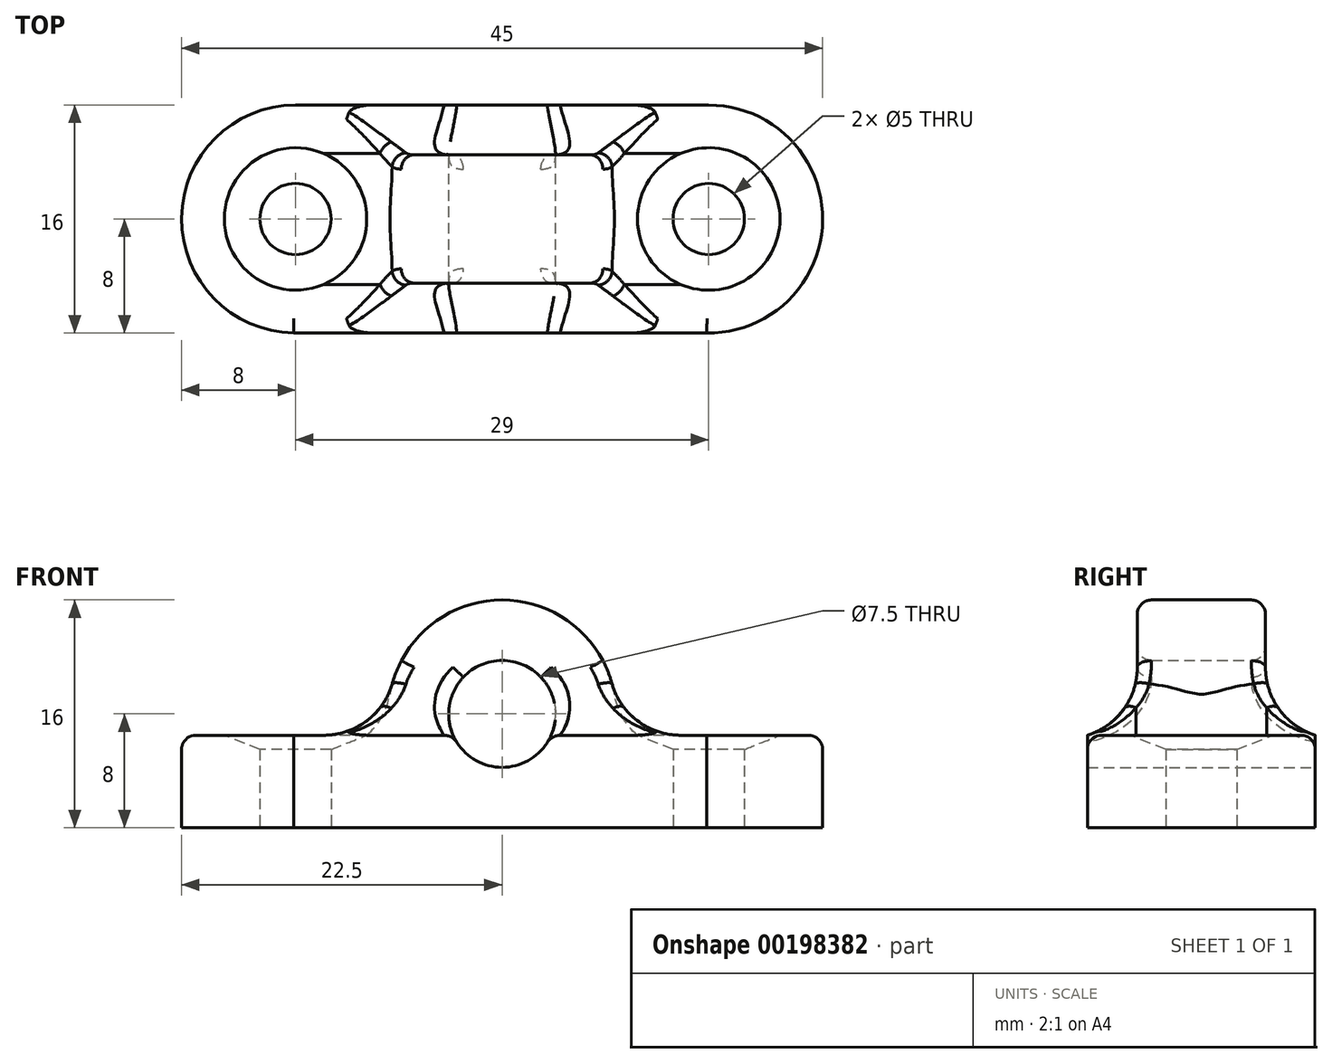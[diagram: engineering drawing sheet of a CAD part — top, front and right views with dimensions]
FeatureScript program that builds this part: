
annotation { "Feature Type Name" : "Feature", "Feature Type Description" : "" }
export const myFeature = defineFeature(function(context is Context, id is Id, definition is map)
    precondition{}
    {
        {
            var Q0;
            Q0=qCreatedBy(makeId("Top.planeOp"),FACE);
            var sketch = newSketch(context, id + "F0", { "sketchPlane" : qUnion([Q0])});
            skCircle(sketch, "E0", {"center": v(-14.5, 0) * mm, "radius": 2.5 * mm});
            skCircle(sketch, "E1", {"center": v(14.5, 0) * mm, "radius": 2.5 * mm});
            skCircle(sketch, "E2", {"center": v(-14.5, 0) * mm, "radius": 8 * mm});
            skCircle(sketch, "E3", {"center": v(14.5, 0) * mm, "radius": 8 * mm});
            skLineSegment(sketch, "E4", {"start": v(-14.63, -8) * mm, "end": v(14.37, -8) * mm});
            skLineSegment(sketch, "E5", {"start": v(-14.5, 8) * mm, "end": v(14.5, 8) * mm});
            skSolve(sketch);
        }
        {
            var Q0;
            Q0=makeQuery(id+"F0.imprint","IMPRINT",FACE,{"disambiguationData":[TD([[makeQuery(id+"F0.imprint","IMPRINT",EDGE,{"derivedFrom":sQuery(id+"F0.wireOp",EDGE,"E0")}),-1.0]])]});
            var Q1;
            {var subQ0=sQuery(id+"F0.wireOp",EDGE,"E5");Q1=makeQuery(id+"F0.imprint","IMPRINT",FACE,{"disambiguationData":[TD([[makeQuery(id+"F0.imprint","IMPRINT",EDGE,{"derivedFrom":subQ0}),-1.0]])]});}
            var Q2;
            Q2=makeQuery(id+"F0.imprint","IMPRINT",FACE,{"disambiguationData":[TD([[makeQuery(id+"F0.imprint","IMPRINT",EDGE,{"derivedFrom":sQuery(id+"F0.wireOp",EDGE,"E1")}),-1.0]])]});
            extrude(context, id + "F1", {"entities" : qUnion([Q0, Q1, Q2]), "depth" : 6.5 * mm});
        }
        {
            var Q0;
            Q0=qCreatedBy(makeId("Front.planeOp"),FACE);
            var sketch = newSketch(context, id + "F2", { "sketchPlane" : qUnion([Q0])});
            skPoint(sketch, "E6", {"position": v(0, 8) * mm});
            skCircle(sketch, "E7", {"center": v(0, 8) * mm, "radius": 8 * mm});
            skCircle(sketch, "E8", {"center": v(0, 8) * mm, "radius": 3.75 * mm});
            skSolve(sketch);
        }
        {
            var Q0;
            Q0=makeQuery(id+"F2.imprint","IMPRINT",FACE,{"disambiguationData":[TD([[makeQuery(id+"F2.imprint","IMPRINT",EDGE,{"derivedFrom":sQuery(id+"F2.wireOp",EDGE,"E7")}),1.0]])]});
            extrude(context, id + "F3", {"entities" : qUnion([Q0]), "operationType" : NewBodyOperationType.ADD, "endBound" : BoundingType.SYMMETRIC, "offsetDistance" : 25 * mm, "depth" : 9 * mm});
        }
        {
            var Q0;
            Q0=makeQuery(id+"F2.imprint","IMPRINT",FACE,{"disambiguationData":[TD([[makeQuery(id+"F2.imprint","IMPRINT",EDGE,{"derivedFrom":sQuery(id+"F2.wireOp",EDGE,"E8")}),1.0]])]});
            extrude(context, id + "F4", {"entities" : qUnion([Q0]), "operationType" : NewBodyOperationType.REMOVE, "endBound" : BoundingType.SYMMETRIC, "oppositeDirection" : true, "depth" : 25 * mm});
        }
        {
            var Q0;
            Q0=makeQuery(id+"F1.opExtrude","CAP_EDGE",EDGE,{"disambiguationData":[OSD([sQuery(id+"F0.wireOp",EDGE,"E0")])],"isStart":false});
            var Q1;
            Q1=makeQuery(id+"F1.opExtrude","CAP_EDGE",EDGE,{"disambiguationData":[OSD([sQuery(id+"F0.wireOp",EDGE,"E1")])],"isStart":false});
            chamfer(context, id + "F5", {"entities" : qUnion([Q0, Q1]), "chamferType" : ChamferType.TWO_OFFSETS, "width1" : 1 * mm, "oppositeDirection" : false, "width2" : 2.5 * mm, "tangentPropagation" : true});
        }
        {
            var Q0;
            Q0=makeQuery(id+"F3.boolean.opBoolean","INTERSECT",EDGE,{"disambiguationData":[OD(0.0)],"derivedFrom":[makeQuery(id+"F1.opExtrude","CAP_FACE",FACE,{"disambiguationData":[OSD([sQuery(id+"F0.wireOp",EDGE,"E0"),sQuery(id+"F0.wireOp",EDGE,"E1"),sQuery(id+"F0.wireOp",EDGE,"E2"),sQuery(id+"F0.wireOp",EDGE,"E3"),sQuery(id+"F0.wireOp",EDGE,"E4"),sQuery(id+"F0.wireOp",EDGE,"E5")])],"isStart":false}),makeQuery(id+"F3.opExtrude","CAP_FACE",FACE,{"disambiguationData":[OSD([sQuery(id+"F2.wireOp",EDGE,"E7"),sQuery(id+"F2.wireOp",EDGE,"E8")])],"isStart":false})]});
            var Q1;
            Q1=makeQuery(id+"F3.boolean.opBoolean","INTERSECT",EDGE,{"disambiguationData":[OD(1.0)],"derivedFrom":[makeQuery(id+"F1.opExtrude","CAP_FACE",FACE,{"disambiguationData":[OSD([sQuery(id+"F0.wireOp",EDGE,"E0"),sQuery(id+"F0.wireOp",EDGE,"E1"),sQuery(id+"F0.wireOp",EDGE,"E2"),sQuery(id+"F0.wireOp",EDGE,"E3"),sQuery(id+"F0.wireOp",EDGE,"E4"),sQuery(id+"F0.wireOp",EDGE,"E5")])],"isStart":false}),makeQuery(id+"F3.opExtrude","CAP_FACE",FACE,{"disambiguationData":[OSD([sQuery(id+"F2.wireOp",EDGE,"E7"),sQuery(id+"F2.wireOp",EDGE,"E8")])],"isStart":false})]});
            var Q2;
            Q2=makeQuery(id+"F3.boolean.opBoolean","INTERSECT",EDGE,{"disambiguationData":[OD(0.0)],"derivedFrom":[makeQuery(id+"F1.opExtrude","CAP_FACE",FACE,{"disambiguationData":[OSD([sQuery(id+"F0.wireOp",EDGE,"E0"),sQuery(id+"F0.wireOp",EDGE,"E1"),sQuery(id+"F0.wireOp",EDGE,"E2"),sQuery(id+"F0.wireOp",EDGE,"E3"),sQuery(id+"F0.wireOp",EDGE,"E4"),sQuery(id+"F0.wireOp",EDGE,"E5")])],"isStart":false}),makeQuery(id+"F3.opExtrude","CAP_FACE",FACE,{"disambiguationData":[OSD([sQuery(id+"F2.wireOp",EDGE,"E7"),sQuery(id+"F2.wireOp",EDGE,"E8")])],"isStart":true})]});
            var Q3;
            Q3=makeQuery(id+"F3.boolean.opBoolean","INTERSECT",EDGE,{"disambiguationData":[OD(1.0)],"derivedFrom":[makeQuery(id+"F1.opExtrude","CAP_FACE",FACE,{"disambiguationData":[OSD([sQuery(id+"F0.wireOp",EDGE,"E0"),sQuery(id+"F0.wireOp",EDGE,"E1"),sQuery(id+"F0.wireOp",EDGE,"E2"),sQuery(id+"F0.wireOp",EDGE,"E3"),sQuery(id+"F0.wireOp",EDGE,"E4"),sQuery(id+"F0.wireOp",EDGE,"E5")])],"isStart":false}),makeQuery(id+"F3.opExtrude","CAP_FACE",FACE,{"disambiguationData":[OSD([sQuery(id+"F2.wireOp",EDGE,"E7"),sQuery(id+"F2.wireOp",EDGE,"E8")])],"isStart":true})]});
            fillet(context, id + "F6", {"entities" : qUnion([Q0, Q1, Q2, Q3]), "radius" : 5 * mm, "tangentPropagation" : true, "allowEdgeOverflow" : false});
        }
        {
            var Q0;
            Q0=makeQuery(id+"F3.boolean.opBoolean","INTERSECT",EDGE,{"disambiguationData":[OD(0.0)],"derivedFrom":[makeQuery(id+"F1.opExtrude","CAP_FACE",FACE,{"disambiguationData":[OSD([sQuery(id+"F0.wireOp",EDGE,"E0"),sQuery(id+"F0.wireOp",EDGE,"E1"),sQuery(id+"F0.wireOp",EDGE,"E2"),sQuery(id+"F0.wireOp",EDGE,"E3"),sQuery(id+"F0.wireOp",EDGE,"E4"),sQuery(id+"F0.wireOp",EDGE,"E5")])],"isStart":false}),makeQuery(id+"F3.opExtrude","SWEPT_FACE",FACE,{"disambiguationData":[OSD([sQuery(id+"F2.wireOp",EDGE,"E7")])]})]});
            var Q1;
            Q1=makeQuery(id+"F3.boolean.opBoolean","INTERSECT",EDGE,{"disambiguationData":[OD(1.0)],"derivedFrom":[makeQuery(id+"F1.opExtrude","CAP_FACE",FACE,{"disambiguationData":[OSD([sQuery(id+"F0.wireOp",EDGE,"E0"),sQuery(id+"F0.wireOp",EDGE,"E1"),sQuery(id+"F0.wireOp",EDGE,"E2"),sQuery(id+"F0.wireOp",EDGE,"E3"),sQuery(id+"F0.wireOp",EDGE,"E4"),sQuery(id+"F0.wireOp",EDGE,"E5")])],"isStart":false}),makeQuery(id+"F3.opExtrude","SWEPT_FACE",FACE,{"disambiguationData":[OSD([sQuery(id+"F2.wireOp",EDGE,"E7")])]})]});
            fillet(context, id + "F7", {"entities" : qUnion([Q0, Q1]), "radius" : 5 * mm, "tangentPropagation" : true, "allowEdgeOverflow" : false});
        }
        {
            var Q0;
            Q0=makeQuery(id+"F3.opExtrude","CAP_EDGE",EDGE,{"disambiguationData":[OSD([sQuery(id+"F2.wireOp",EDGE,"E8")])],"isStart":true});
            var Q1;
            Q1=makeQuery(id+"F3.opExtrude","CAP_EDGE",EDGE,{"disambiguationData":[OSD([sQuery(id+"F2.wireOp",EDGE,"E8")])],"isStart":false});
            fillet(context, id + "F8", {"entities" : qUnion([Q0, Q1]), "radius" : 1 * mm, "tangentPropagation" : true, "allowEdgeOverflow" : false});
        }
        {
            var Q0;
            Q0=makeQuery(id+"F3.opExtrude","CAP_EDGE",EDGE,{"disambiguationData":[OSD([sQuery(id+"F2.wireOp",EDGE,"E7")])],"isStart":true});
            var Q1;
            Q1=makeQuery(id+"F3.opExtrude","CAP_EDGE",EDGE,{"disambiguationData":[OSD([sQuery(id+"F2.wireOp",EDGE,"E7")])],"isStart":false});
            fillet(context, id + "F9", {"entities" : qUnion([Q0, Q1]), "radius" : 1 * mm, "tangentPropagation" : true, "allowEdgeOverflow" : false});
        }
    });
